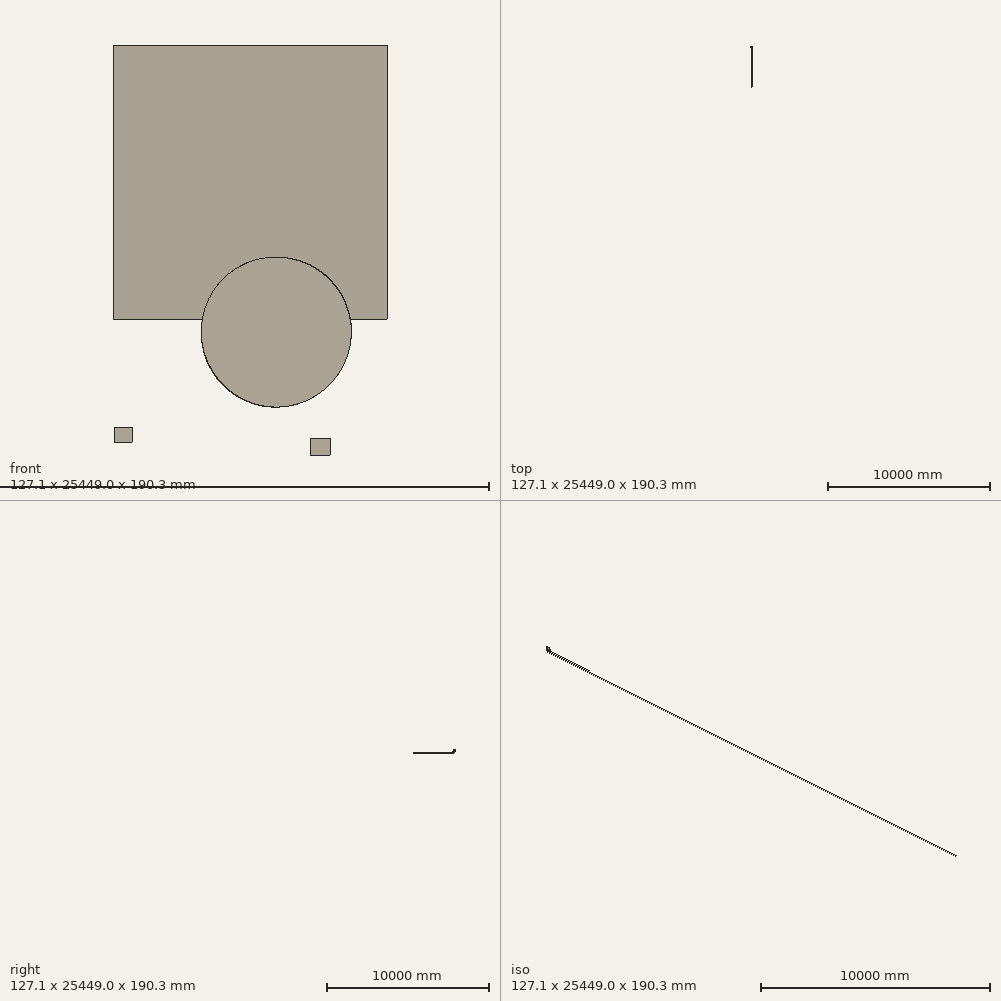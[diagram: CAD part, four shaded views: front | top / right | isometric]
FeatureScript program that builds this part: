
annotation { "Feature Type Name" : "Feature", "Feature Type Description" : "" }
export const myFeature = defineFeature(function(context is Context, id is Id, definition is map)
    precondition{}
    {
        {
            var Q0;
            Q0=qCreatedBy(makeId("Front.planeOp"),FACE);
            var sketch = newSketch(context, id + "F0", { "sketchPlane" : qUnion([Q0])});
            skCircle(sketch, "E0", {"center": v(15.93, -6.05) * mm, "radius": 34.87 * mm});
            skSolve(sketch);
        }
        {
            var Q0;
            Q0=qCreatedBy(makeId("Front.planeOp"),FACE);
            var sketch = newSketch(context, id + "F1", { "sketchPlane" : qUnion([Q0])});
            skLineSegment(sketch, "E1.bottom", {"start": v(-21.91, -5.23) * mm, "end": v(-67.75, -5.23) * mm});
            skLineSegment(sketch, "E1.top", {"start": v(-21.91, 43.62) * mm, "end": v(-67.75, 43.62) * mm});
            skLineSegment(sketch, "E1.left", {"start": v(-21.91, -5.23) * mm, "end": v(-21.91, 43.62) * mm});
            skLineSegment(sketch, "E1.right", {"start": v(-67.75, -5.23) * mm, "end": v(-67.75, 43.62) * mm});
            skLineSegment(sketch, "E2.bottom", {"start": v(-34.58, -47.85) * mm, "end": v(-48.65, -47.85) * mm});
            skLineSegment(sketch, "E2.top", {"start": v(-34.58, -27.94) * mm, "end": v(-48.65, -27.94) * mm});
            skLineSegment(sketch, "E2.left", {"start": v(-34.58, -47.85) * mm, "end": v(-34.58, -27.94) * mm});
            skLineSegment(sketch, "E2.right", {"start": v(-48.65, -47.85) * mm, "end": v(-48.65, -27.94) * mm});
            skLineSegment(sketch, "E3.bottom", {"start": v(41.21, -55.48) * mm, "end": v(31.96, -55.48) * mm});
            skLineSegment(sketch, "E3.top", {"start": v(41.21, -63.32) * mm, "end": v(31.96, -63.32) * mm});
            skLineSegment(sketch, "E3.left", {"start": v(41.21, -55.48) * mm, "end": v(41.21, -63.32) * mm});
            skLineSegment(sketch, "E3.right", {"start": v(31.96, -55.48) * mm, "end": v(31.96, -63.32) * mm});
            skSolve(sketch);
        }
        {
            var Q0;
            Q0=qCreatedBy(makeId("Top.planeOp"),FACE);
            var sketch = newSketch(context, id + "F2", { "sketchPlane" : qUnion([Q0])});
            skLineSegment(sketch, "E4", {"start": v(-35.18, -8.44) * mm, "end": v(0, 48.96) * mm});
            skLineSegment(sketch, "E5", {"start": v(0, 48.96) * mm, "end": v(26.64, -9.32) * mm});
            skLineSegment(sketch, "E6", {"start": v(26.64, -9.32) * mm, "end": v(29.53, -8) * mm});
            skLineSegment(sketch, "E7", {"start": v(29.53, -8) * mm, "end": v(67.48, -57.8) * mm});
            skLineSegment(sketch, "E8", {"start": v(67.48, -57.8) * mm, "end": v(-59.6, -53.93) * mm});
            skLineSegment(sketch, "E9", {"start": v(-59.6, -53.93) * mm, "end": v(-41.27, -9.32) * mm});
            skLineSegment(sketch, "E10", {"start": v(-41.27, -9.32) * mm, "end": v(-35.18, -8.44) * mm});
            skLineSegment(sketch, "E11", {"start": v(0, 48.96) * mm, "end": v(37.6, -18.6) * mm});
            skLineSegment(sketch, "E12", {"start": v(0, 48.96) * mm, "end": v(-43.92, -5.25) * mm});
            skLineSegment(sketch, "E13", {"start": v(-41.27, -6.07) * mm, "end": v(-41.27, -8.44) * mm});
            skLineSegment(sketch, "E14", {"start": v(-41.27, -8.44) * mm, "end": v(-43.92, -5.25) * mm});
            skSolve(sketch);
        }
        {
            var Q0;
            Q0=makeQuery(id+"F2.imprint","IMPRINT",FACE,{"disambiguationData":[TD([[makeQuery(id+"F2.imprint","IMPRINT",EDGE,{"derivedFrom":sQuery(id+"F2.wireOp",EDGE,"E4")}),-1.0]])]});
            extrude(context, id + "F3", {"entities" : qUnion([Q0]), "depth" : 127 * mm});
        }
        {
            var Q0;
            Q0=makeQuery(id+"F0.imprint","IMPRINT",FACE,{"disambiguationData":[TD([[makeQuery(id+"F0.imprint","IMPRINT",EDGE,{"derivedFrom":sQuery(id+"F0.wireOp",EDGE,"E0")}),1.0]])]});
            extrude(context, id + "F4", {"entities" : qUnion([Q0]), "operationType" : NewBodyOperationType.ADD, "depth" : 127 * mm});
        }
        {
            var Q0;
            Q0=makeQuery(id+"F1.imprint","IMPRINT",FACE,{"disambiguationData":[TD([[makeQuery(id+"F1.imprint","IMPRINT",EDGE,{"derivedFrom":sQuery(id+"F1.wireOp",EDGE,"E3.bottom")}),1.0]])]});
            extrude(context, id + "F5", {"entities" : qUnion([Q0]), "depth" : 2540 * mm});
        }
        {
            var Q0;
            Q0=qCreatedBy(makeId("Front.planeOp"),FACE);
            var sketch = newSketch(context, id + "F6", { "sketchPlane" : qUnion([Q0])});
            skLineSegment(sketch, "E15.bottom", {"start": v(-59.14, -57.4) * mm, "end": v(-51.04, -57.4) * mm});
            skLineSegment(sketch, "E15.top", {"start": v(-59.14, -50.1) * mm, "end": v(-51.04, -50.1) * mm});
            skLineSegment(sketch, "E15.left", {"start": v(-59.14, -57.4) * mm, "end": v(-59.14, -50.1) * mm});
            skLineSegment(sketch, "E15.right", {"start": v(-51.04, -57.4) * mm, "end": v(-51.04, -50.1) * mm});
            skSolve(sketch);
        }
        {
            var Q0;
            Q0=makeQuery(id+"F6.imprint","IMPRINT",FACE,{"disambiguationData":[TD([[makeQuery(id+"F6.imprint","IMPRINT",EDGE,{"derivedFrom":sQuery(id+"F6.wireOp",EDGE,"E15.bottom")}),1.0]])]});
            extrude(context, id + "F7", {"entities" : qUnion([Q0]), "depth" : 25400 * mm});
        }
    });
